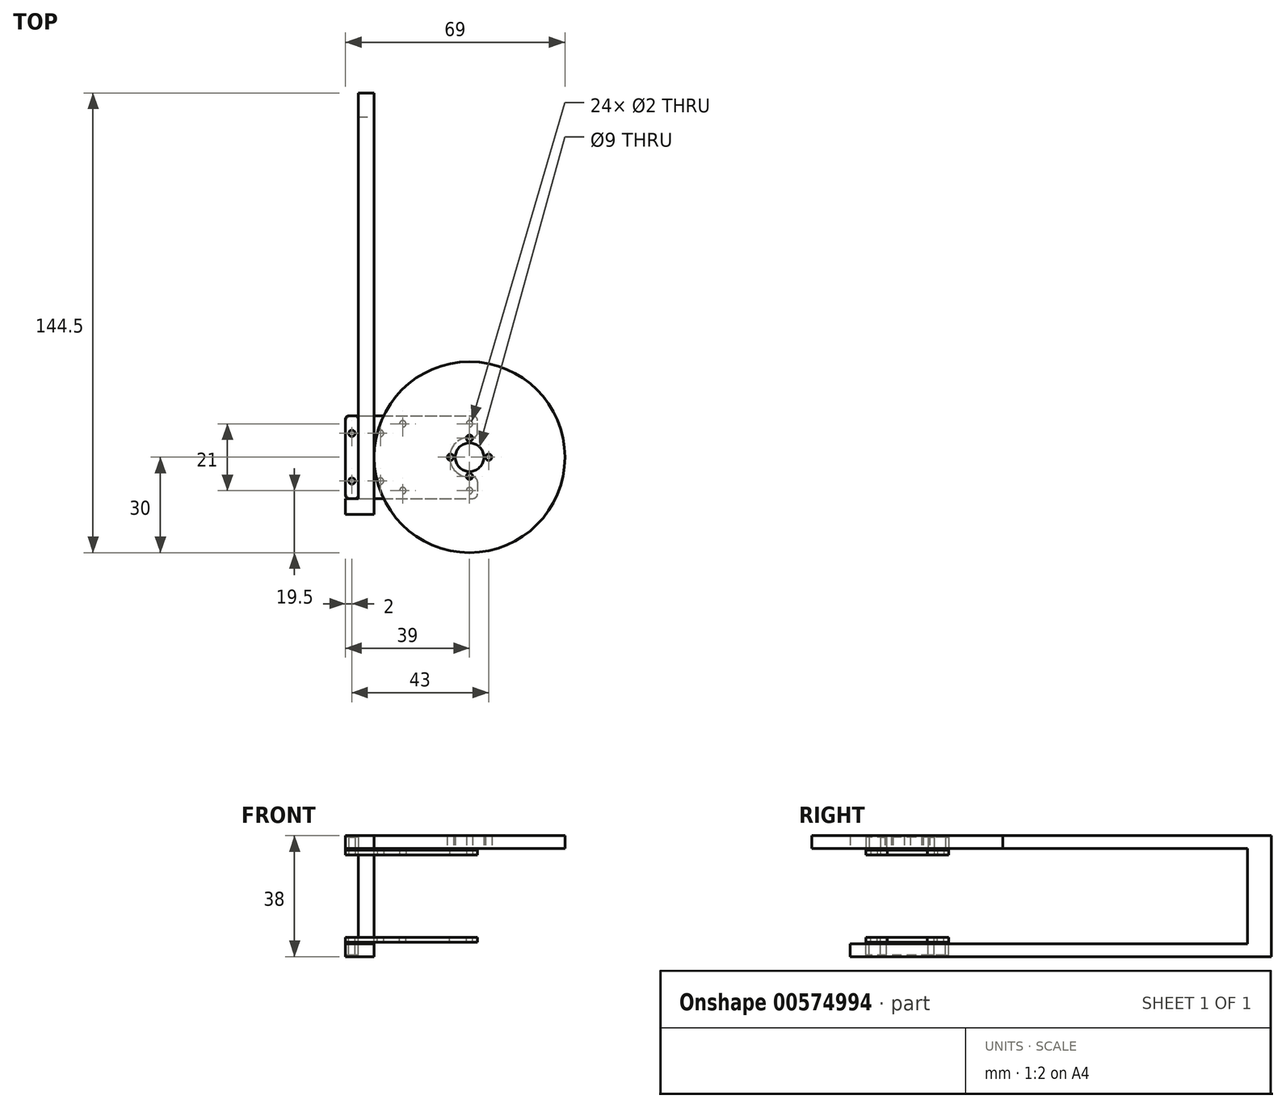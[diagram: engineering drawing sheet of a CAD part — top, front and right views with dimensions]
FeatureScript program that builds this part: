
annotation { "Feature Type Name" : "Feature", "Feature Type Description" : "" }
export const myFeature = defineFeature(function(context is Context, id is Id, definition is map)
    precondition{}
    {
        {
            var Q0;
            Q0=qCreatedBy(makeId("Top.planeOp"),FACE);
            var sketch = newSketch(context, id + "F0", { "sketchPlane" : qUnion([Q0])});
            skLineSegment(sketch, "E0.bottom", {"start": v(18.5, 13) * mm, "end": v(-7.5, 13) * mm});
            skLineSegment(sketch, "E0.top", {"start": v(18.5, -13) * mm, "end": v(-7.5, -13) * mm});
            skLineSegment(sketch, "E0.left", {"start": v(18.5, 13) * mm, "end": v(18.5, -13) * mm, "construction": true});
            skLineSegment(sketch, "E0.right", {"start": v(-7.5, 13) * mm, "end": v(-7.5, -13) * mm, "construction": true});
            skPoint(sketch, "E0.middle", {"position": v(5.5, 0) * mm});
            skCircle(sketch, "E1", {"center": v(-5, 0) * mm, "radius": 30 * mm, "construction": true});
            skCircle(sketch, "E2", {"center": v(30, 0) * mm, "radius": 5 * mm, "construction": true});
            skPoint(sketch, "E3", {"position": v(0, 0) * mm});
            skPoint(sketch, "E4", {"position": v(-35, 0) * mm});
            skPoint(sketch, "E5", {"position": v(35, 0) * mm});
            skLineSegment(sketch, "E6.bottom", {"start": v(-35, -32) * mm, "end": v(35, -32) * mm, "construction": true});
            skLineSegment(sketch, "E6.top", {"start": v(-35, 93) * mm, "end": v(35, 93) * mm, "construction": true});
            skLineSegment(sketch, "E6.left", {"start": v(-35, -32) * mm, "end": v(-35, 93) * mm, "construction": true});
            skLineSegment(sketch, "E6.right", {"start": v(35, -32) * mm, "end": v(35, 93) * mm, "construction": true});
            skPoint(sketch, "E7", {"position": v(-5, -30) * mm});
            skPoint(sketch, "E8", {"position": v(-5, 30) * mm});
            skCircle(sketch, "E9", {"center": v(-5, 10.5) * mm, "radius": 1 * mm});
            skCircle(sketch, "E10.1.0", {"center": v(-5, -10.5) * mm, "radius": 1 * mm});
            skCircle(sketch, "E10.2.0", {"center": v(16, -10.5) * mm, "radius": 1 * mm});
            skCircle(sketch, "E11.1.3.0", {"center": v(16, 10.5) * mm, "radius": 1 * mm});
            skLineSegment(sketch, "E12.bottom", {"start": v(-42, 13) * mm, "end": v(-40, 13) * mm});
            skLineSegment(sketch, "E12.top", {"start": v(-42, -13) * mm, "end": v(-40, -13) * mm});
            skLineSegment(sketch, "E12.left", {"start": v(-44, 11) * mm, "end": v(-44, -11) * mm});
            skLineSegment(sketch, "E12.right", {"start": v(-40, 13) * mm, "end": v(-40, -13) * mm});
            skLineSegment(sketch, "E13", {"start": v(-42, 13) * mm, "end": v(-42, -13) * mm, "construction": true});
            skLineSegment(sketch, "E14", {"start": v(-40, 13) * mm, "end": v(-7.5, 13) * mm});
            skLineSegment(sketch, "E15", {"start": v(-40, -13) * mm, "end": v(-7.5, -13) * mm});
            skCircle(sketch, "E16", {"center": v(-42, 7.5) * mm, "radius": 1 * mm});
            skArc(sketch, "E17", {"start": v(-5, 6.25) * mm, "mid": v(-11.25, 0) * mm, "end": v(-5, -6.25) * mm});
            skCircle(sketch, "E18.MirrorC", {"center": v(-42, -7.5) * mm, "radius": 1 * mm});
            skLineSegment(sketch, "E19.bottom", {"start": v(40, 13) * mm, "end": v(42, 13) * mm});
            skLineSegment(sketch, "E19.top", {"start": v(40, -13) * mm, "end": v(42, -13) * mm});
            skLineSegment(sketch, "E19.left", {"start": v(40, 13) * mm, "end": v(40, -13) * mm});
            skLineSegment(sketch, "E19.right", {"start": v(44, 11) * mm, "end": v(44, -11) * mm});
            skCircle(sketch, "E20", {"center": v(42, 7.5) * mm, "radius": 1 * mm});
            skPoint(sketch, "E20.centerSnap0", {"position": v(42, 13) * mm});
            skCircle(sketch, "E21.MirrorC", {"center": v(42, -7.5) * mm, "radius": 1 * mm});
            skLineSegment(sketch, "E22", {"start": v(18.5, 13) * mm, "end": v(40, 13) * mm});
            skLineSegment(sketch, "E23", {"start": v(18.5, -13) * mm, "end": v(40, -13) * mm});
            skCircle(sketch, "E24", {"center": v(30, 0) * mm, "radius": 1.55 * mm});
            skPoint(sketch, "E25.visualSharp", {"position": v(-44, 13) * mm});
            skArc(sketch, "E25.filletArc", {"start": v(-42, 13) * mm, "mid": v(-43.41, 12.41) * mm, "end": v(-44, 11) * mm});
            skPoint(sketch, "E26.visualSharp", {"position": v(-44, -13) * mm});
            skArc(sketch, "E26.filletArc", {"start": v(-44, -11) * mm, "mid": v(-43.41, -12.41) * mm, "end": v(-42, -13) * mm});
            skPoint(sketch, "E27.visualSharp", {"position": v(44, 13) * mm});
            skArc(sketch, "E27.filletArc", {"start": v(44, 11) * mm, "mid": v(43.41, 12.41) * mm, "end": v(42, 13) * mm});
            skPoint(sketch, "E28.visualSharp", {"position": v(44, -13) * mm});
            skArc(sketch, "E28.filletArc", {"start": v(42, -13) * mm, "mid": v(43.41, -12.41) * mm, "end": v(44, -11) * mm});
            skLineSegment(sketch, "E29", {"start": v(-44, 0) * mm, "end": v(44, 0) * mm, "construction": true});
            skLineSegment(sketch, "E30", {"start": v(-5, -10.5) * mm, "end": v(-5, 10.5) * mm, "construction": true});
            skCircle(sketch, "E31.MirrorC", {"center": v(-26, -10.5) * mm, "radius": 1 * mm});
            skCircle(sketch, "E32.MirrorC", {"center": v(-26, 10.5) * mm, "radius": 1 * mm});
            skLineSegment(sketch, "E33", {"start": v(-2.5, -6.25) * mm, "end": v(-2.5, -13) * mm});
            skLineSegment(sketch, "E34", {"start": v(-5, -6.25) * mm, "end": v(-2.5, -6.25) * mm});
            skPoint(sketch, "E34.endSnap0", {"position": v(-2.5, -9.36) * mm});
            skPoint(sketch, "E35.orphan", {"position": v(-2.5, -5.73) * mm});
            skLineSegment(sketch, "E36.MirrorCS", {"start": v(-5, 6.25) * mm, "end": v(-2.5, 6.25) * mm});
            skLineSegment(sketch, "E37.MirrorCS", {"start": v(-2.5, 6.25) * mm, "end": v(-2.5, 13) * mm});
            skLineSegment(sketch, "E38", {"start": v(-40, 7.5) * mm, "end": v(-35, 7.5) * mm, "construction": true});
            skLineSegment(sketch, "E39", {"start": v(-37.5, 13) * mm, "end": v(-37.5, -13) * mm, "construction": true});
            skPoint(sketch, "E39.startSnap0", {"position": v(-37.5, 7.5) * mm});
            skCircle(sketch, "E40.MirrorC", {"center": v(-33, -7.5) * mm, "radius": 1 * mm});
            skCircle(sketch, "E41.MirrorC", {"center": v(-33, 7.5) * mm, "radius": 1 * mm});
            skSolve(sketch);
        }
        {
            var Q0;
            Q0=makeQuery(id+"F0.imprint","IMPRINT",FACE,{"disambiguationData":[TD([[makeQuery(id+"F0.imprint","IMPRINT",EDGE,{"derivedFrom":sQuery(id+"F0.wireOp",EDGE,"E12.bottom")}),-1.0]])]});
            var Q1;
            Q1=makeQuery(id+"F0.imprint","IMPRINT",FACE,{"disambiguationData":[TD([[makeQuery(id+"F0.imprint","IMPRINT",EDGE,{"derivedFrom":sQuery(id+"F0.wireOp",EDGE,"E9")}),-1.0]])]});
            extrude(context, id + "F1", {"entities" : qUnion([Q0, Q1]), "depth" : 1.5 * mm, "offsetDistance" : 25 * mm});
        }
        {
            var Q0;
            Q0=makeQuery(id+"F1.opExtrude","CAP_FACE",FACE,{"disambiguationData":[OSD([sQuery(id+"F0.wireOp",EDGE,"E0.bottom"),sQuery(id+"F0.wireOp",EDGE,"E0.top"),sQuery(id+"F0.wireOp",EDGE,"E9"),sQuery(id+"F0.wireOp",EDGE,"E10.1.0"),sQuery(id+"F0.wireOp",EDGE,"E10.2.0"),sQuery(id+"F0.wireOp",EDGE,"E11.1.3.0"),sQuery(id+"F0.wireOp",EDGE,"E12.bottom"),sQuery(id+"F0.wireOp",EDGE,"E12.top"),sQuery(id+"F0.wireOp",EDGE,"E12.left"),sQuery(id+"F0.wireOp",EDGE,"E14"),sQuery(id+"F0.wireOp",EDGE,"E15"),sQuery(id+"F0.wireOp",EDGE,"E16"),sQuery(id+"F0.wireOp",EDGE,"E17"),sQuery(id+"F0.wireOp",EDGE,"E18.MirrorC"),sQuery(id+"F0.wireOp",EDGE,"E19.bottom"),sQuery(id+"F0.wireOp",EDGE,"E19.top"),sQuery(id+"F0.wireOp",EDGE,"E19.right"),sQuery(id+"F0.wireOp",EDGE,"E20"),sQuery(id+"F0.wireOp",EDGE,"E21.MirrorC"),sQuery(id+"F0.wireOp",EDGE,"E22"),sQuery(id+"F0.wireOp",EDGE,"E23"),sQuery(id+"F0.wireOp",EDGE,"E24"),sQuery(id+"F0.wireOp",EDGE,"E25.filletArc"),sQuery(id+"F0.wireOp",EDGE,"E26.filletArc"),sQuery(id+"F0.wireOp",EDGE,"E27.filletArc"),sQuery(id+"F0.wireOp",EDGE,"E28.filletArc")])],"isStart":false});
            var sketch = newSketch(context, id + "F2", { "sketchPlane" : qUnion([Q0])});
            skCircle(sketch, "E42.0", {"center": v(-5, 0) * mm, "radius": 30 * mm});
            skPoint(sketch, "E43.0", {"position": v(-44, 13) * mm});
            skPoint(sketch, "E44.0", {"position": v(-40, -13) * mm});
            skCircle(sketch, "E45.0", {"center": v(-42, -7.5) * mm, "radius": 1 * mm});
            skCircle(sketch, "E46.0", {"center": v(-42, 7.5) * mm, "radius": 1 * mm});
            skLineSegment(sketch, "E47.bottom", {"start": v(-43, 13) * mm, "end": v(-41, 13) * mm});
            skLineSegment(sketch, "E47.top", {"start": v(-43, -13) * mm, "end": v(-41, -13) * mm});
            skLineSegment(sketch, "E47.left", {"start": v(-44, 12) * mm, "end": v(-44, -12) * mm});
            skLineSegment(sketch, "E47.right", {"start": v(-40, 12) * mm, "end": v(-40, -12) * mm});
            skArc(sketch, "E48.filletArc", {"start": v(-43, 13) * mm, "mid": v(-43.7, 12.7) * mm, "end": v(-44, 12) * mm});
            skPoint(sketch, "E49.visualSharp", {"position": v(-40, 13) * mm});
            skArc(sketch, "E49.filletArc", {"start": v(-40, 12) * mm, "mid": v(-40.3, 12.7) * mm, "end": v(-41, 13) * mm});
            skPoint(sketch, "E50.visualSharp", {"position": v(-44, -13) * mm});
            skArc(sketch, "E50.filletArc", {"start": v(-44, -12) * mm, "mid": v(-43.7, -12.7) * mm, "end": v(-43, -13) * mm});
            skArc(sketch, "E51.filletArc", {"start": v(-41, -13) * mm, "mid": v(-40.3, -12.7) * mm, "end": v(-40, -12) * mm});
            skCircle(sketch, "E52", {"center": v(-5, 0) * mm, "radius": 4.5 * mm});
            skCircle(sketch, "E53", {"center": v(-11, 0) * mm, "radius": 1 * mm});
            skCircle(sketch, "E54.1.0", {"center": v(-5, -6) * mm, "radius": 1 * mm});
            skCircle(sketch, "E54.2.0", {"center": v(1, 0) * mm, "radius": 1 * mm});
            skCircle(sketch, "E55.1.3.0", {"center": v(-5, 6) * mm, "radius": 1 * mm});
            skSolve(sketch);
        }
        {
            var Q0;
            Q0 = qSketchRegion(id + "F2", true);
            extrude(context, id + "F3", {"entities" : qUnion([Q0]), "depth" : 4 * mm, "offsetDistance" : 25 * mm});
        }
        {
            var Q0;
            Q0=makeQuery(id+"F1.opExtrude","SWEPT_EDGE",EDGE,{"disambiguationData":[OSD([sQuery(id+"F0.wireOp",EDGE,"E0.top"),sQuery(id+"F0.wireOp",EDGE,"E33")])]});
            var Q1;
            Q1=makeQuery(id+"F1.opExtrude","SWEPT_EDGE",EDGE,{"disambiguationData":[OSD([sQuery(id+"F0.wireOp",EDGE,"E33"),sQuery(id+"F0.wireOp",EDGE,"E34")])]});
            var Q2;
            Q2=makeQuery(id+"F1.opExtrude","SWEPT_EDGE",EDGE,{"disambiguationData":[OSD([sQuery(id+"F0.wireOp",EDGE,"E36.MirrorCS"),sQuery(id+"F0.wireOp",EDGE,"E37.MirrorCS")])]});
            var Q3;
            Q3=makeQuery(id+"F1.opExtrude","SWEPT_EDGE",EDGE,{"disambiguationData":[OSD([sQuery(id+"F0.wireOp",EDGE,"E0.bottom"),sQuery(id+"F0.wireOp",EDGE,"E37.MirrorCS")])]});
            fillet(context, id + "F4", {"entities" : qUnion([Q0, Q1, Q2, Q3]), "tangentPropagation" : true, "radius" : 1.5 * mm, "defaultsChanged" : false, "vertexSettings" : [], "allowEdgeOverflow" : false});
        }
        {
            var Q0;
            Q0=makeQuery(id+"F3.opExtrude","SWEPT_BODY",BODY,{"disambiguationData":[OSD([sQuery(id+"F2.wireOp",EDGE,"E42.0"),sQuery(id+"F2.wireOp",EDGE,"E52"),sQuery(id+"F2.wireOp",EDGE,"E53"),sQuery(id+"F2.wireOp",EDGE,"E54.1.0"),sQuery(id+"F2.wireOp",EDGE,"E54.2.0"),sQuery(id+"F2.wireOp",EDGE,"E55.1.3.0")])]});
            transform(context, id + "F5", {"entities" : qUnion([Q0]), "transformType" : TransformType.TRANSLATION_3D, "dx" : 0 * mm, "dy" : 0 * mm, "dz" : 0.5 * mm, "makeCopy" : false});
        }
        {
            var Q0;
            Q0=makeQuery(id+"F1.opExtrude","CAP_FACE",FACE,{"disambiguationData":[OSD([sQuery(id+"F0.wireOp",EDGE,"E0.bottom"),sQuery(id+"F0.wireOp",EDGE,"E0.top"),sQuery(id+"F0.wireOp",EDGE,"E9"),sQuery(id+"F0.wireOp",EDGE,"E10.1.0"),sQuery(id+"F0.wireOp",EDGE,"E10.2.0"),sQuery(id+"F0.wireOp",EDGE,"E11.1.3.0"),sQuery(id+"F0.wireOp",EDGE,"E12.bottom"),sQuery(id+"F0.wireOp",EDGE,"E12.top"),sQuery(id+"F0.wireOp",EDGE,"E12.left"),sQuery(id+"F0.wireOp",EDGE,"E14"),sQuery(id+"F0.wireOp",EDGE,"E15"),sQuery(id+"F0.wireOp",EDGE,"E16"),sQuery(id+"F0.wireOp",EDGE,"E17"),sQuery(id+"F0.wireOp",EDGE,"E18.MirrorC"),sQuery(id+"F0.wireOp",EDGE,"E19.bottom"),sQuery(id+"F0.wireOp",EDGE,"E19.top"),sQuery(id+"F0.wireOp",EDGE,"E19.right"),sQuery(id+"F0.wireOp",EDGE,"E20"),sQuery(id+"F0.wireOp",EDGE,"E21.MirrorC"),sQuery(id+"F0.wireOp",EDGE,"E22"),sQuery(id+"F0.wireOp",EDGE,"E23"),sQuery(id+"F0.wireOp",EDGE,"E24"),sQuery(id+"F0.wireOp",EDGE,"E25.filletArc"),sQuery(id+"F0.wireOp",EDGE,"E26.filletArc"),sQuery(id+"F0.wireOp",EDGE,"E27.filletArc"),sQuery(id+"F0.wireOp",EDGE,"E28.filletArc")])],"isStart":true});
            cPlane(context, id + "F6", {"entities" : qUnion([Q0]), "cplaneType" : CPlaneType.OFFSET, "offset" : 13 * mm, "width" : 150 * mm, "height" : 150 * mm});
        }
        {
            var Q0;
            Q0=makeQuery(id+"F1.opExtrude","SWEPT_BODY",BODY,{"disambiguationData":[OSD([sQuery(id+"F0.wireOp",EDGE,"E0.bottom"),sQuery(id+"F0.wireOp",EDGE,"E0.top"),sQuery(id+"F0.wireOp",EDGE,"E9"),sQuery(id+"F0.wireOp",EDGE,"E10.1.0"),sQuery(id+"F0.wireOp",EDGE,"E10.2.0"),sQuery(id+"F0.wireOp",EDGE,"E11.1.3.0"),sQuery(id+"F0.wireOp",EDGE,"E12.bottom"),sQuery(id+"F0.wireOp",EDGE,"E12.top"),sQuery(id+"F0.wireOp",EDGE,"E12.left"),sQuery(id+"F0.wireOp",EDGE,"E14"),sQuery(id+"F0.wireOp",EDGE,"E15"),sQuery(id+"F0.wireOp",EDGE,"E16"),sQuery(id+"F0.wireOp",EDGE,"E17"),sQuery(id+"F0.wireOp",EDGE,"E18.MirrorC"),sQuery(id+"F0.wireOp",EDGE,"E19.bottom"),sQuery(id+"F0.wireOp",EDGE,"E19.top"),sQuery(id+"F0.wireOp",EDGE,"E19.right"),sQuery(id+"F0.wireOp",EDGE,"E20"),sQuery(id+"F0.wireOp",EDGE,"E21.MirrorC"),sQuery(id+"F0.wireOp",EDGE,"E22"),sQuery(id+"F0.wireOp",EDGE,"E23"),sQuery(id+"F0.wireOp",EDGE,"E24"),sQuery(id+"F0.wireOp",EDGE,"E25.filletArc"),sQuery(id+"F0.wireOp",EDGE,"E26.filletArc"),sQuery(id+"F0.wireOp",EDGE,"E27.filletArc"),sQuery(id+"F0.wireOp",EDGE,"E28.filletArc")])]});
            var Q1;
            Q1=makeQuery(id+"F3.opExtrude","SWEPT_BODY",BODY,{"disambiguationData":[OSD([sQuery(id+"F2.wireOp",EDGE,"E45.0"),sQuery(id+"F2.wireOp",EDGE,"E46.0"),sQuery(id+"F2.wireOp",EDGE,"E47.bottom"),sQuery(id+"F2.wireOp",EDGE,"E47.top"),sQuery(id+"F2.wireOp",EDGE,"E47.left"),sQuery(id+"F2.wireOp",EDGE,"E47.right"),sQuery(id+"F2.wireOp",EDGE,"E48.filletArc"),sQuery(id+"F2.wireOp",EDGE,"E49.filletArc"),sQuery(id+"F2.wireOp",EDGE,"E50.filletArc"),sQuery(id+"F2.wireOp",EDGE,"E51.filletArc")])]});
            var Q2;
            Q2=qCreatedBy(id+"F6.planeOp",FACE);
            mirror(context, id + "F7", {"entities" : qUnion([Q0, Q1]), "mirrorPlane" : qUnion([Q2])});
        }
        {
            var Q0;
            Q0=makeQuery(id+"F3.opExtrude","CAP_FACE",FACE,{"disambiguationData":[OSD([sQuery(id+"F2.wireOp",EDGE,"E42.0"),sQuery(id+"F2.wireOp",EDGE,"E52"),sQuery(id+"F2.wireOp",EDGE,"E53"),sQuery(id+"F2.wireOp",EDGE,"E54.1.0"),sQuery(id+"F2.wireOp",EDGE,"E54.2.0"),sQuery(id+"F2.wireOp",EDGE,"E55.1.3.0")])],"isStart":true});
            var sketch = newSketch(context, id + "F8", { "sketchPlane" : qUnion([Q0])});
            skLineSegment(sketch, "E56.bottom", {"start": v(-40, 18) * mm, "end": v(-35, 18) * mm});
            skLineSegment(sketch, "E56.top", {"start": v(-40, -107) * mm, "end": v(-35, -107) * mm});
            skLineSegment(sketch, "E56.left", {"start": v(-40, 13) * mm, "end": v(-40, -107) * mm});
            skLineSegment(sketch, "E56.right", {"start": v(-35, 18) * mm, "end": v(-35, -107) * mm});
            skPoint(sketch, "E57", {"position": v(-35, 0) * mm});
            skPoint(sketch, "E58.0", {"position": v(-42, 13) * mm});
            skLineSegment(sketch, "E59", {"start": v(-40, 13) * mm, "end": v(-44, 13) * mm});
            skLineSegment(sketch, "E60", {"start": v(-44, 13) * mm, "end": v(-44, 18) * mm});
            skLineSegment(sketch, "E61", {"start": v(-44, 18) * mm, "end": v(-40, 18) * mm});
            skPoint(sketch, "E62.0", {"position": v(-44, 12) * mm});
            skLineSegment(sketch, "E63", {"start": v(-40, -107) * mm, "end": v(-40, -114.5) * mm});
            skLineSegment(sketch, "E64", {"start": v(-40, -114.5) * mm, "end": v(-35, -114.5) * mm});
            skLineSegment(sketch, "E65", {"start": v(-35, -114.5) * mm, "end": v(-35, -107) * mm});
            skSolve(sketch);
        }
        {
            var Q0;
            Q0 = qSketchRegion(id + "F8", true);
            extrude(context, id + "F9", {"entities" : qUnion([Q0]), "oppositeDirection" : true, "depth" : 4 * mm, "offsetDistance" : 25 * mm});
        }
        {
            var Q0;
            Q0=makeQuery(id+"F8.imprint","IMPRINT",FACE,{"disambiguationData":[TD([[makeQuery(id+"F8.imprint","IMPRINT",EDGE,{"derivedFrom":sQuery(id+"F8.wireOp",EDGE,"E56.top")}),-1.0]])]});
            var Q1;
            Q1=qCreatedBy(id+"F6.planeOp",FACE);
            extrude(context, id + "F10", {"entities" : qUnion([Q0]), "operationType" : NewBodyOperationType.ADD, "endBound" : BoundingType.UP_TO_SURFACE, "depth" : 25 * mm, "endBoundEntityFace" : qUnion([Q1]), "offsetDistance" : 25 * mm});
        }
        {
            var Q0;
            Q0=makeQuery(id+"F9.opExtrude","SWEPT_BODY",BODY,{"disambiguationData":[OSD([sQuery(id+"F8.wireOp",EDGE,"E56.bottom"),sQuery(id+"F8.wireOp",EDGE,"E56.left"),sQuery(id+"F8.wireOp",EDGE,"E56.right"),sQuery(id+"F8.wireOp",EDGE,"E59"),sQuery(id+"F8.wireOp",EDGE,"E60"),sQuery(id+"F8.wireOp",EDGE,"E61"),sQuery(id+"F8.wireOp",EDGE,"E63"),sQuery(id+"F8.wireOp",EDGE,"E64"),sQuery(id+"F8.wireOp",EDGE,"E65")])]});
            var Q1;
            Q1=qCreatedBy(id+"F6.planeOp",FACE);
            mirror(context, id + "F11", {"operationType" : NewBodyOperationType.ADD, "entities" : qUnion([Q0]), "mirrorPlane" : qUnion([Q1])});
        }
    });
